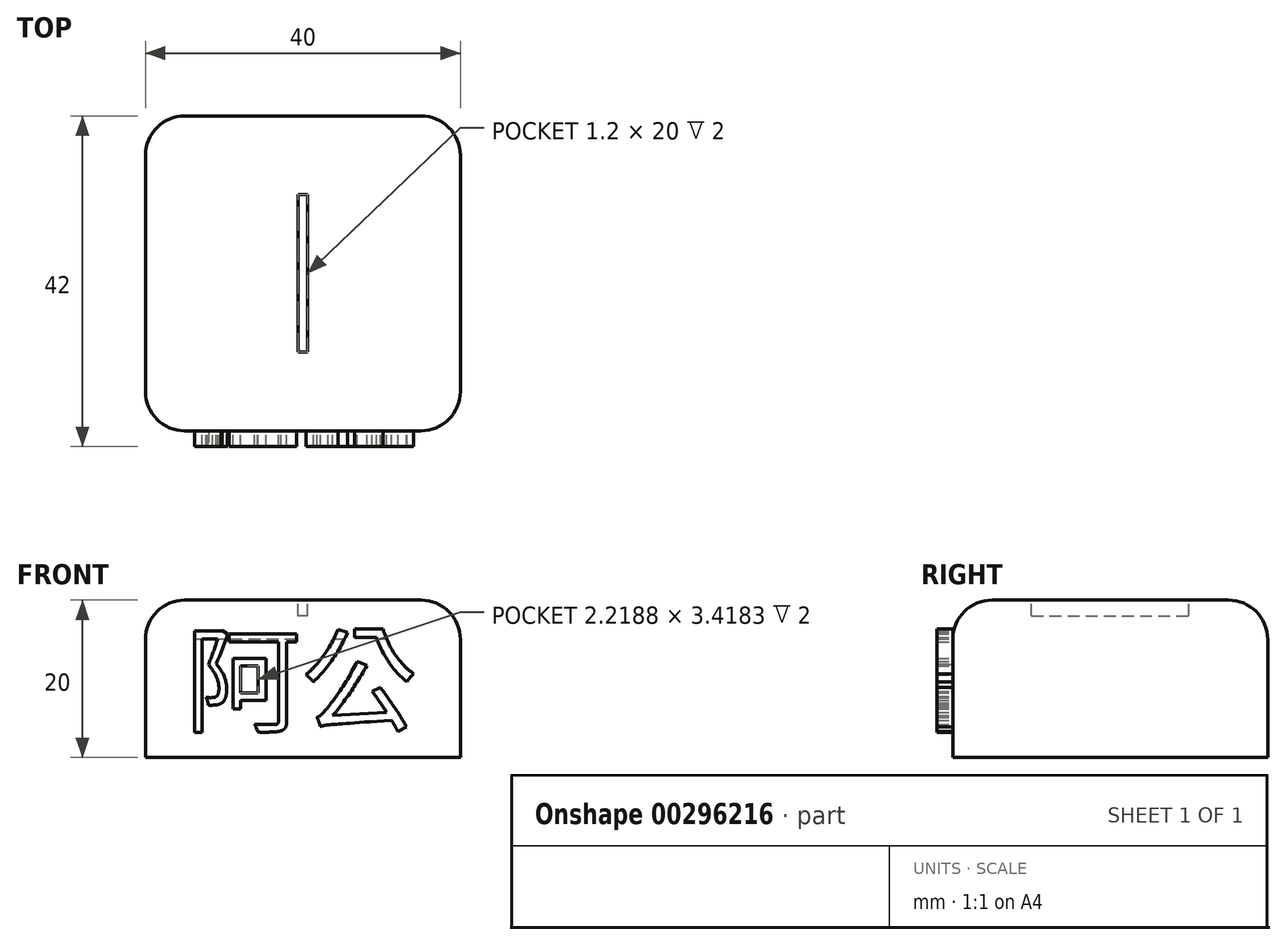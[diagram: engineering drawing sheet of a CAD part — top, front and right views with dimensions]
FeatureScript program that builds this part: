
annotation { "Feature Type Name" : "Feature", "Feature Type Description" : "" }
export const myFeature = defineFeature(function(context is Context, id is Id, definition is map)
    precondition{}
    {
        {
            var Q0;
            Q0=qCreatedBy(makeId("Top.planeOp"),FACE);
            var sketch = newSketch(context, id + "F0", { "sketchPlane" : qUnion([Q0])});
            skLineSegment(sketch, "E0.bottom", {"start": v(20, -20) * mm, "end": v(-20, -20) * mm});
            skLineSegment(sketch, "E0.top", {"start": v(20, 20) * mm, "end": v(-20, 20) * mm});
            skLineSegment(sketch, "E0.left", {"start": v(20, -20) * mm, "end": v(20, 20) * mm});
            skLineSegment(sketch, "E0.right", {"start": v(-20, -20) * mm, "end": v(-20, 20) * mm});
            skPoint(sketch, "E0.middle", {"position": v(0, 0) * mm});
            skLineSegment(sketch, "E1.bottom", {"start": v(0.6, -10) * mm, "end": v(-0.6, -10) * mm});
            skLineSegment(sketch, "E1.top", {"start": v(0.6, 10) * mm, "end": v(-0.6, 10) * mm});
            skLineSegment(sketch, "E1.left", {"start": v(0.6, -10) * mm, "end": v(0.6, 10) * mm});
            skLineSegment(sketch, "E1.right", {"start": v(-0.6, -10) * mm, "end": v(-0.6, 10) * mm});
            skSolve(sketch);
        }
        {
            var Q0;
            Q0=makeQuery(id+"F0.imprint","IMPRINT",FACE,{"disambiguationData":[TD([[makeQuery(id+"F0.imprint","IMPRINT",EDGE,{"derivedFrom":sQuery(id+"F0.wireOp",EDGE,"E0.bottom")}),-1.0]])]});
            var Q1;
            Q1=makeQuery(id+"F0.imprint","IMPRINT",FACE,{"disambiguationData":[TD([[makeQuery(id+"F0.imprint","IMPRINT",EDGE,{"derivedFrom":sQuery(id+"F0.wireOp",EDGE,"E1.bottom")}),-1.0]])]});
            extrude(context, id + "F1", {"entities" : qUnion([Q0, Q1]), "oppositeDirection" : true, "depth" : 20 * mm});
        }
        {
            var Q0;
            Q0=makeQuery(id+"F0.imprint","IMPRINT",FACE,{"disambiguationData":[TD([[makeQuery(id+"F0.imprint","IMPRINT",EDGE,{"derivedFrom":sQuery(id+"F0.wireOp",EDGE,"E1.bottom")}),-1.0]])]});
            extrude(context, id + "F2", {"entities" : qUnion([Q0]), "operationType" : NewBodyOperationType.REMOVE, "oppositeDirection" : true, "depth" : 2 * mm});
        }
        {
            var Q0;
            Q0=makeQuery(id+"F2.boolean.opBoolean","COPY",EDGE,{"derivedFrom":makeQuery(id+"F2.opExtrude","CAP_EDGE",EDGE,{"disambiguationData":[OSD([sQuery(id+"F0.wireOp",EDGE,"E1.left")])],"isStart":true})});
            var Q1;
            Q1=makeQuery(id+"F2.boolean.opBoolean","COPY",EDGE,{"derivedFrom":makeQuery(id+"F2.opExtrude","CAP_EDGE",EDGE,{"disambiguationData":[OSD([sQuery(id+"F0.wireOp",EDGE,"E1.right")])],"isStart":true})});
            var Q2;
            Q2=makeQuery(id+"F1.opExtrude","SWEPT_EDGE",EDGE,{"disambiguationData":[OSD([sQuery(id+"F0.wireOp",EDGE,"E0.bottom"),sQuery(id+"F0.wireOp",EDGE,"E0.left")])]});
            var Q3;
            Q3=makeQuery(id+"F1.opExtrude","SWEPT_EDGE",EDGE,{"disambiguationData":[OSD([sQuery(id+"F0.wireOp",EDGE,"E0.top"),sQuery(id+"F0.wireOp",EDGE,"E0.left")])]});
            var Q4;
            Q4=makeQuery(id+"F1.opExtrude","CAP_EDGE",EDGE,{"disambiguationData":[OSD([sQuery(id+"F0.wireOp",EDGE,"E0.left")])],"isStart":true});
            var Q5;
            Q5=makeQuery(id+"F1.opExtrude","SWEPT_EDGE",EDGE,{"disambiguationData":[OSD([sQuery(id+"F0.wireOp",EDGE,"E0.bottom"),sQuery(id+"F0.wireOp",EDGE,"E0.right")])]});
            var Q6;
            Q6=makeQuery(id+"F1.opExtrude","SWEPT_EDGE",EDGE,{"disambiguationData":[OSD([sQuery(id+"F0.wireOp",EDGE,"E0.top"),sQuery(id+"F0.wireOp",EDGE,"E0.right")])]});
            var Q7;
            Q7=makeQuery(id+"F1.opExtrude","CAP_EDGE",EDGE,{"disambiguationData":[OSD([sQuery(id+"F0.wireOp",EDGE,"E0.top")])],"isStart":true});
            var Q8;
            Q8=makeQuery(id+"F1.opExtrude","CAP_EDGE",EDGE,{"disambiguationData":[OSD([sQuery(id+"F0.wireOp",EDGE,"E0.right")])],"isStart":true});
            var Q9;
            Q9=makeQuery(id+"F1.opExtrude","CAP_EDGE",EDGE,{"disambiguationData":[OSD([sQuery(id+"F0.wireOp",EDGE,"E0.bottom")])],"isStart":true});
            fillet(context, id + "F3", {"entities" : qUnion([Q0, Q1, Q2, Q3, Q4, Q5, Q6, Q7, Q8, Q9]), "radius" : 5 * mm, "tangentPropagation" : true, "allowEdgeOverflow" : false});
        }
        {
            var Q0;
            Q0=makeQuery(id+"F1.opExtrude","SWEPT_FACE",FACE,{"disambiguationData":[OSD([sQuery(id+"F0.wireOp",EDGE,"E0.bottom")])]});
            var sketch = newSketch(context, id + "F4", { "sketchPlane" : qUnion([Q0])});
            skText(sketch, "E2", { "text": "阿公", "fontName": "NotoSansCJKtc-Regular.otf"});
            const initialGuessF4  = {"E2": [-0.015, -0.01565, 1, 0, 0.01065]};
            skSetInitialGuess(sketch, initialGuessF4);
            skSolve(sketch);
        }
        {
            var Q0;
            {var subQ1=sQuery(id+"F4.wireOp",EDGE,"E2.sketch_text.stroke-7");Q0=makeQuery(id+"F4.imprint","IMPRINT",FACE,{"disambiguationData":[TD([[makeQuery(id+"F4.imprint","IMPRINT",EDGE,{"derivedFrom":subQ1}),1.0]])]});}
            var Q1;
            Q1=makeQuery(id+"F4.imprint","IMPRINT",FACE,{"disambiguationData":[TD([[makeQuery(id+"F4.imprint","IMPRINT",EDGE,{"derivedFrom":sQuery(id+"F4.wireOp",EDGE,"E2.sketch_text.stroke-0")}),1.0]])]});
            var Q2;
            {var subQ0=sQuery(id+"F4.wireOp",EDGE,"E2.sketch_text.stroke-3");Q2=makeQuery(id+"F4.imprint","IMPRINT",FACE,{"disambiguationData":[TD([[makeQuery(id+"F4.imprint","IMPRINT",EDGE,{"derivedFrom":subQ0}),1.0]])]});}
            var Q3;
            {var subQ0=sQuery(id+"F4.wireOp",EDGE,"E2.sketch_text.stroke-28");Q3=makeQuery(id+"F4.imprint","IMPRINT",FACE,{"disambiguationData":[TD([[makeQuery(id+"F4.imprint","IMPRINT",EDGE,{"derivedFrom":subQ0}),1.0]])]});}
            var Q4;
            {var subQ1=sQuery(id+"F4.wireOp",EDGE,"E2.sketch_text.stroke-30");Q4=makeQuery(id+"F4.imprint","IMPRINT",FACE,{"disambiguationData":[TD([[makeQuery(id+"F4.imprint","IMPRINT",EDGE,{"derivedFrom":subQ1}),1.0]])]});}
            var Q5;
            Q5=makeQuery(id+"F4.imprint","IMPRINT",FACE,{"disambiguationData":[TD([[makeQuery(id+"F4.imprint","IMPRINT",EDGE,{"derivedFrom":sQuery(id+"F4.wireOp",EDGE,"E2.sketch_text.stroke-18")}),1.0]])]});
            var Q6;
            {var subQ0=sQuery(id+"F4.wireOp",EDGE,"E2.sketch_text.stroke-41");Q6=makeQuery(id+"F4.imprint","IMPRINT",FACE,{"disambiguationData":[TD([[makeQuery(id+"F4.imprint","IMPRINT",EDGE,{"derivedFrom":subQ0}),1.0]])]});}
            var Q7;
            {var subQ0=sQuery(id+"F4.wireOp",EDGE,"E2.sketch_text.stroke-43");Q7=makeQuery(id+"F4.imprint","IMPRINT",FACE,{"disambiguationData":[TD([[makeQuery(id+"F4.imprint","IMPRINT",EDGE,{"derivedFrom":subQ0}),1.0]])]});}
            var Q8;
            Q8=makeQuery(id+"F4.imprint","IMPRINT",FACE,{"disambiguationData":[TD([[makeQuery(id+"F4.imprint","IMPRINT",EDGE,{"derivedFrom":sQuery(id+"F4.wireOp",EDGE,"E2.sketch_text.stroke-56")}),1.0]])]});
            var Q9;
            {var subQ0=sQuery(id+"F4.wireOp",EDGE,"E2.sketch_text.stroke-59");Q9=makeQuery(id+"F4.imprint","IMPRINT",FACE,{"disambiguationData":[TD([[makeQuery(id+"F4.imprint","IMPRINT",EDGE,{"derivedFrom":subQ0}),1.0]])]});}
            var Q10;
            Q10=makeQuery(id+"F4.imprint","IMPRINT",FACE,{"disambiguationData":[TD([[makeQuery(id+"F4.imprint","IMPRINT",EDGE,{"derivedFrom":sQuery(id+"F4.wireOp",EDGE,"E2.sketch_text.stroke-44")}),1.0]])]});
            extrude(context, id + "F5", {"entities" : qUnion([Q0, Q1, Q2, Q3, Q4, Q5, Q6, Q7, Q8, Q9, Q10]), "operationType" : NewBodyOperationType.ADD, "depth" : 2 * mm});
        }
    });
